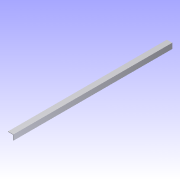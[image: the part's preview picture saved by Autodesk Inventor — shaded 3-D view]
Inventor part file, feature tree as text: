
AUTODESK INVENTOR PART (.ipt)
format: ipt  version: 2012 (Build 160160000, 160)  size: 68,096 bytes
history: native  units: in
note: dims shown in document units (in); Inventor stores cm internally (conversion verified against a paired STEP export)
features: extrude x1, sketch x1
ambient origin geometry x8: Origin, YZ Plane, XZ Plane, XY Plane, X Axis, Y Axis, Z Axis, Center Point
bodies: Solid1 (feature_tree)
feature tree (2):
  extrude  "Extrusion1"  Depth=1.5in
  sketch  "Sketch1"  dims[d0=1.5in d1=1.5in d2=0.125in d3=0.125in d4=44.25in d5=0.0in]
